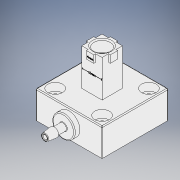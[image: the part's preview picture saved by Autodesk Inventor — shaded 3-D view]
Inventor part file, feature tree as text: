
AUTODESK INVENTOR PART (.ipt)
format: ipt  version: 2019 (Build 230136000, 136)  size: 599,040 bytes
history: native  units: mm
features: sketch x11, extrude x6, plane x3, projected_geometry x3, revolve x2, fillet x2, sweep x1, hole x1, pattern_circular x1
ambient origin geometry x8: Origin, YZ Plane, XZ Plane, XY Plane, X Axis, Y Axis, Z Axis, Center Point
bodies: Solid1 (feature_tree)
feature tree (30):
  revolve  "Revolution1"  [1 undecoded]
  plane  "Work Plane1"
  extrude  "Extrusion1"  Depth=0.75mm
  plane  "Work Plane7"
  extrude  "Extrusion6"  Depth=0.75mm
  extrude  "Extrusion7"  TaperAngle=0.0deg  [1 undecoded]
  sketch  "Sketch17"  dims[d14=2.0mm d15=0.0mm d45=0.0mm d47=15.0mm d48=0.0mm]
  plane  "Work Plane8"
  sweep  "Sweep3"
  fillet  "Fillet1"  Radius=15.0mm
  hole  "Hole3"  [1 undecoded]
  revolve  "Revolution2"  [1 undecoded]
  fillet  "Fillet2"  [1 undecoded]
  extrude  "Extrusion13"  Depth=25.4mm
  pattern_circular  "Circular Pattern1"  [2 undecoded]
  sketch  "Sketch29"  dims[d72=4.496mm d73=6.0mm d74=7.938mm d75=4.166mm d76=90.0deg d77=19.05mm d78=20.594885mm]
  sketch  "Sketch30"  dims[d79=3.0mm d80=6.0mm d81=5.0mm d82=1.8796mm d83=0.25mm d84=2.413mm d85=5.08mm d86=1.15mm d87=0.25mm d88=0.25mm d89=90.0deg d90=0.5mm d124=0.0mm d125=0.0mm d126=4.0mm d127=1.0mm d128=0.0mm d129=40.0mm d130=360.0deg d133=5.5mm d134=1.013632mm d135=0.5mm d136=0.0mm d137=0.5mm d138=0.0mm d139=1.0mm d140=0.125mm d141=0.125mm d142=0.125mm d143=3.25mm]
  extrude  "Extrusion14"  Depth=5.0mm
  extrude  "Extrusion15"  Depth=1.8796mm
  sketch  "Sketch1"  dims[d1=20.0mm d5=9.0mm]
  sketch  "Sketch2"  dims[d6=0.35mm d7=0.75mm]
  sketch  "Sketch11"  dims[d8=0.75mm d9=0.75mm]
  sketch  "Sketch16"  dims[d10=90.0deg d11=0.0mm]
  projected_geometry  "Projected Loop9"
  sketch  "Sketch18"  dims[d60=36.0mm d61=36.0mm]
  sketch  "Sketch19"  dims[d64=8.45mm d65=32.7mm d66=0.0mm d67=0.0mm d68=0.0mm]
  sketch  "Sketch21"  dims[d69=3.0mm d70=25.4mm]
  sketch  "Sketch28"  dims[d71=25.4mm]
  projected_geometry  "Projected Loop13"
  projected_geometry  "Projected Loop14"
note: 7 required parameter values undecoded (feature->parameter linkage not recoverable at this tier; creation-order binding heuristic only, values carry confidence <= 0.55)